# Revit family: Toilet_Tissue_Dispenser-Bradley_Corp-5412
name_source: partatom
category: Specialty Equipment
revit_build: Autodesk Revit MEP 2012 (Build: 20110309_2315(x64)
units: mm (PartAtom-declared; Revit-internal decimal feet)

## types (1)
- 5412
    ADA Compliant = Yes
    Assembly Code = C1030200
    Buy American Act = To Be Determined
    Default Elevation = 48 "
    Depth = 5.313 "
    Description = Toilet Tissue Dispenser
    Height = 10.375 "
    Low Emitting Material = No
    Manufacturer = Bradley Corporation
    MasterFormat Number = 10 28 00
    MasterFormat Title = Toilet, Bath, and Laundry Accessories
    Model = 5412
    OmniClass Table 21 Number = 21-03 10 90 40
    OmniClass Table 21 Title = Toilet, Bath, and Laundry Accessories
    OmniClass Table 23 Number = 23.31.25.21
    OmniClass Table 23 Title = Toilet Paper Dispensers
    Percentage of Recycled Content = 0
    Product Tech Data URL - English = http://bradleycorp.com
    Recess Depth = 4 "
    Specifications URL = http://www.bradleycorp.com
    Spindle Material = Plastic - Bradley Corp - Polyethylene - Gray
    URL = http://www.bradleycorp.com
    Unit Material = Metal - Bradley Corp - Stainless Steel - Satin
    Version = 2.0
    Warranty Information = Complete Unit 1 Year Warranty. This Warranty does not cover installation or any other labor charges and does not apply to any units which have been damaged by abuse, improper installation, imporper maintanence, or altered in any way.
    Width = 5.563 "

## geometry (parser evidence)
native form markers: Blend x6, Sweep x1
no freeform markers — native parametric forms only
